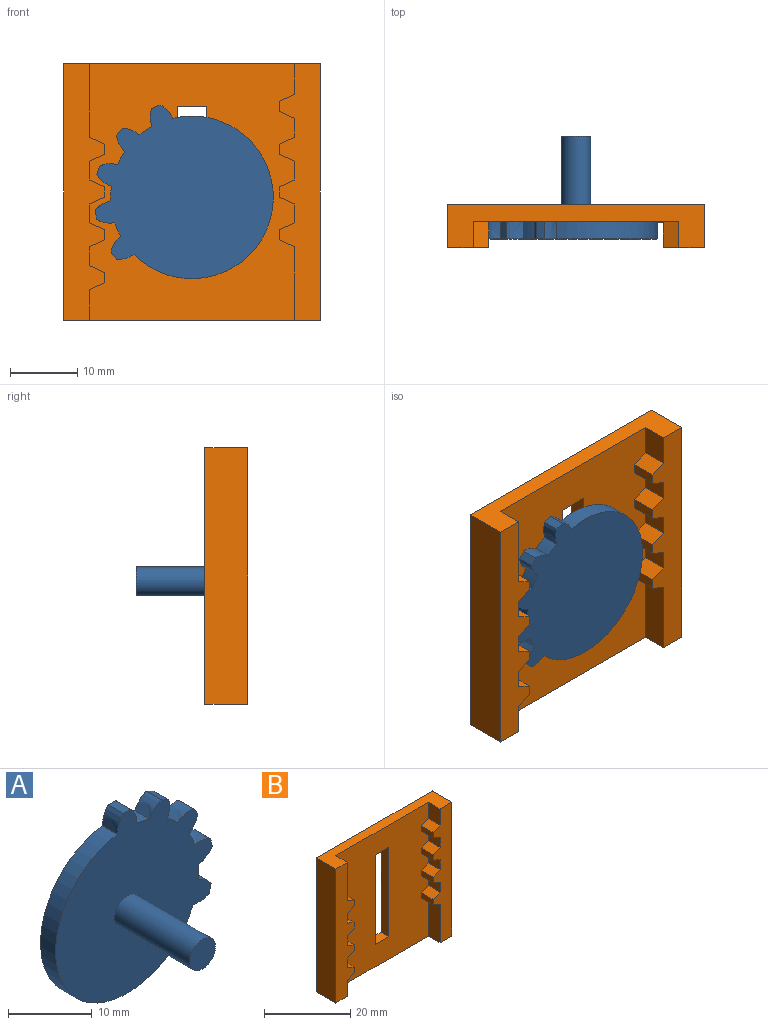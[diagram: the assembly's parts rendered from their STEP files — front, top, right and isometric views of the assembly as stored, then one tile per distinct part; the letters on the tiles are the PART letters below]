
ASSEMBLY  parts=2 mates=2
PART A: 24 faces, bbox 26.4x15.2x26.5 mm
  f0: cylinder r=12.06mm len=24.01mm, axis (0,1,0), area 127.9mm2, adj f5,f6,f9,f19
  f1: cylinder r=12.06mm len=2.54mm, axis (0,1,0), area 5.5mm2, adj f5,f6,f16,f21
  f2: cylinder r=12.06mm len=2.54mm, axis (0,1,0), area 5.5mm2, adj f5,f6,f13,f18
  f3: cylinder r=12.06mm len=2.54mm, axis (0,1,0), area 5.5mm2, adj f5,f6,f10,f15
  f4: cylinder r=12.06mm len=2.54mm, axis (0,1,0), area 5.5mm2, adj f5,f6,f7,f12
  f5: plane 26.54x26.39mm, normal (0,-1,0), area 475.3mm2, adj f0,f1,f2,f3,f4,f7,f8,f9
  f6: plane 26.54x26.39mm, normal (0,1,0), area 490mm2, adj f0,f1,f2,f3,f4,f7,f8,f9
  f7: extruded ~2.54x2.53mm, area 7.1mm2, adj f4,f5,f6,f8
  f8: plane 2.54x1.27mm, normal (0,0,1), area 3.2mm2, adj f5,f6,f7,f9
  f9: extruded ~2.54x2.53mm, area 7.1mm2, adj f0,f5,f6,f8
  f10: extruded ~2.73x2.54mm, area 7.1mm2, adj f3,f5,f6,f11
  f11: plane 2.54x1.14mm, normal (0.44,0,0.9), area 3.2mm2, adj f5,f6,f10,f12
  f12: extruded ~2.54x2.05mm, area 7.1mm2, adj f4,f5,f6,f11
  f13: extruded ~2.54x2.36mm, area 7.1mm2, adj f2,f5,f6,f14
  f14: plane 2.54x1.01mm, normal (0.79,0,0.61), area 3.2mm2, adj f5,f6,f13,f15
  f15: extruded ~2.64x2.54mm, area 7.1mm2, adj f3,f5,f6,f14
  f16: extruded ~2.54x2.28mm, area 7.1mm2, adj f1,f5,f6,f17
  f17: plane 2.54x1.25mm, normal (0.98,0,0.2), area 3.2mm2, adj f5,f6,f16,f18
  f18: extruded ~2.68x2.54mm, area 7.1mm2, adj f2,f5,f6,f17
  f19: extruded ~2.71x2.54mm, area 7.1mm2, adj f0,f5,f6,f20
  f20: plane 2.54x1.23mm, normal (0.97,0,-0.26), area 3.2mm2, adj f5,f6,f19,f21
  f21: extruded ~2.54x2.17mm, area 7.1mm2, adj f1,f5,f6,f20
  f22: cylinder r=2.16mm len=12.7mm, axis (0,1,0), area 172.3mm2, adj f5,f23
  f23: plane 4.32x4.32mm, normal (0,-1,0), area 14.6mm2, adj f22
PART B: 46 faces, bbox 38.1x6.4x38.1 mm
  f0: plane 4.57x3.81mm, normal (-1,0,0), area 17.4mm2, adj f1,f9,f17,f43
  f1: plane 38.1x30.48mm, normal (0,-1,0), area 1001.9mm2, adj f0,f2,f3,f4,f5,f6,f7,f8
  f2: plane 3.81x2.79mm, normal (-1,0,0), area 10.6mm2, adj f1,f17,f40,f45
  f3: plane 3.81x2.79mm, normal (-1,0,0), area 10.6mm2, adj f1,f17,f27,f37
  f4: plane 10.92x3.81mm, normal (1,0,0), area 41.6mm2, adj f1,f9,f15,f36
  f5: plane 3.81x2.79mm, normal (1,0,0), area 10.6mm2, adj f1,f15,f28,f33
  f6: plane 3.81x2.79mm, normal (1,0,0), area 10.6mm2, adj f1,f15,f22,f30
  f7: plane 3.81x2.79mm, normal (-1,0,0), area 10.6mm2, adj f1,f17,f25,f42
  f8: plane 3.81x2.79mm, normal (1,0,0), area 10.6mm2, adj f1,f15,f24,f34
  f9: plane 38.1x6.35mm, normal (0,0,1), area 125.8mm2, adj f0,f1,f4,f10,f12,f13,f15,f17
  f10: plane 38.1x6.35mm, normal (-1,0,0), area 241.9mm2, adj f9,f11,f13,f15
  f11: plane 38.1x6.35mm, normal (0,0,-1), area 125.8mm2, adj f1,f10,f12,f13,f14,f15,f16,f17
  f12: plane 38.1x6.35mm, normal (1,0,0), area 241.9mm2, adj f9,f11,f13,f17
  f13: plane 38.1x38.1mm, normal (0,1,0), area 1338.7mm2, adj f9,f10,f11,f12,f18,f19,f20,f21
  f14: plane 4.57x3.81mm, normal (1,0,0), area 17.4mm2, adj f1,f11,f15,f31
  f15: plane 38.1x6.1mm, normal (0,-1,0), area 168.4mm2, adj f4,f5,f6,f8,f9,f10,f11,f14
  f16: plane 10.92x3.81mm, normal (-1,0,0), area 41.6mm2, adj f1,f11,f17,f39
  f17: plane 38.1x6.1mm, normal (0,-1,0), area 168.4mm2, adj f0,f2,f3,f7,f9,f11,f12,f16
  f18: plane 25.4x2.54mm, normal (1,0,0), area 64.5mm2, adj f1,f13,f19,f21
  f19: plane 4.45x2.54mm, normal (0,0,1), area 11.3mm2, adj f1,f13,f18,f20
  f20: plane 25.4x2.54mm, normal (-1,0,0), area 64.5mm2, adj f1,f13,f19,f21
  f21: plane 4.45x2.54mm, normal (0,0,-1), area 11.3mm2, adj f1,f13,f18,f20
  f22: plane 3.81x2.29mm, normal (0.41,0,-0.91), area 9.5mm2, adj f1,f6,f15,f23
  f23: plane 3.81x1.52mm, normal (1,0,0), area 5.8mm2, adj f1,f15,f22,f24
  f24: plane 3.81x2.29mm, normal (0.41,0,0.91), area 9.5mm2, adj f1,f8,f15,f23
  f25: plane 3.81x2.29mm, normal (-0.41,0,0.91), area 9.5mm2, adj f1,f7,f17,f26
  f26: plane 3.81x1.52mm, normal (-1,0,0), area 5.8mm2, adj f1,f17,f25,f27
  f27: plane 3.81x2.29mm, normal (-0.41,0,-0.91), area 9.5mm2, adj f1,f3,f17,f26
  f28: plane 3.81x2.29mm, normal (0.41,0,-0.91), area 9.5mm2, adj f1,f5,f15,f29
  f29: plane 3.81x1.52mm, normal (1,0,0), area 5.8mm2, adj f1,f15,f28,f30
  f30: plane 3.81x2.29mm, normal (0.41,0,0.91), area 9.5mm2, adj f1,f6,f15,f29
  f31: plane 3.81x2.29mm, normal (0.41,0,-0.91), area 9.5mm2, adj f1,f14,f15,f32
  f32: plane 3.81x1.52mm, normal (1,0,0), area 5.8mm2, adj f1,f15,f31,f33
  f33: plane 3.81x2.29mm, normal (0.41,0,0.91), area 9.5mm2, adj f1,f5,f15,f32
  f34: plane 3.81x2.29mm, normal (0.41,0,-0.91), area 9.5mm2, adj f1,f8,f15,f35
  f35: plane 3.81x1.52mm, normal (1,0,0), area 5.8mm2, adj f1,f15,f34,f36
  f36: plane 3.81x2.29mm, normal (0.41,0,0.91), area 9.5mm2, adj f1,f4,f15,f35
  f37: plane 3.81x2.29mm, normal (-0.41,0,0.91), area 9.5mm2, adj f1,f3,f17,f38
  f38: plane 3.81x1.52mm, normal (-1,0,0), area 5.8mm2, adj f1,f17,f37,f39
  f39: plane 3.81x2.29mm, normal (-0.41,0,-0.91), area 9.5mm2, adj f1,f16,f17,f38
  f40: plane 3.81x2.29mm, normal (-0.41,0,0.91), area 9.5mm2, adj f1,f2,f17,f41
  f41: plane 3.81x1.52mm, normal (-1,0,0), area 5.8mm2, adj f1,f17,f40,f42
  f42: plane 3.81x2.29mm, normal (-0.41,0,-0.91), area 9.5mm2, adj f1,f7,f17,f41
  f43: plane 3.81x2.29mm, normal (-0.41,0,0.91), area 9.5mm2, adj f0,f1,f17,f44
  f44: plane 3.81x1.52mm, normal (-1,0,0), area 5.8mm2, adj f1,f17,f43,f45
  f45: plane 3.81x2.29mm, normal (-0.41,0,-0.91), area 9.5mm2, adj f1,f2,f17,f44
PLACE A rot(axis=(0.19,0,-0.98),180deg) t=(2.9,2.52,3.33)mm
PLACE B t=(2.9,7.6,4.13)mm fixed
MATE planar A.f5 <-> B.f1  axis (0,1,0) through (2.2,5.06,3.53)mm
MATE pin_slot A.f22 <-> B.f1  axis (0,-1,0) through (2.9,5.06,3.33)mm
